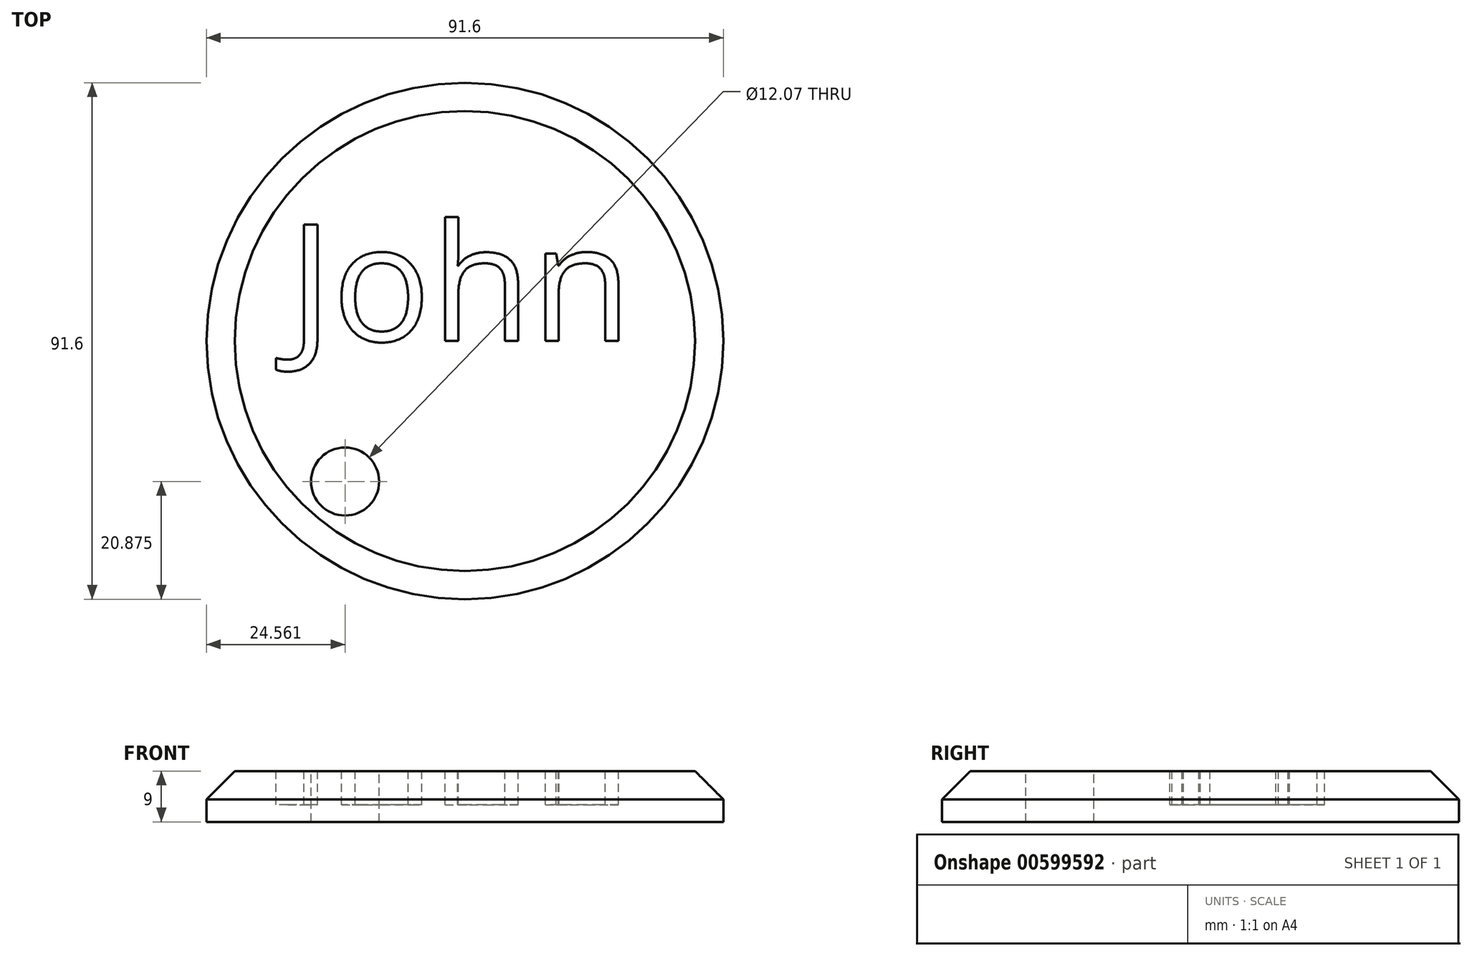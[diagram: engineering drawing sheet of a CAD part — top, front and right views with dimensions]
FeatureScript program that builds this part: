
annotation { "Feature Type Name" : "Feature", "Feature Type Description" : "" }
export const myFeature = defineFeature(function(context is Context, id is Id, definition is map)
    precondition{}
    {
        {
            var Q0;
            Q0=qCreatedBy(makeId("Top.planeOp"),FACE);
            var sketch = newSketch(context, id + "F0", { "sketchPlane" : qUnion([Q0])});
            skCircle(sketch, "E0", {"center": v(0, 0) * mm, "radius": 45.8 * mm});
            skSolve(sketch);
        }
        {
            var Q0;
            Q0=makeQuery(id+"F0.imprint","IMPRINT",FACE,{"disambiguationData":[TD([[makeQuery(id+"F0.imprint","IMPRINT",EDGE,{"derivedFrom":sQuery(id+"F0.wireOp",EDGE,"E0")}),1.0]])]});
            extrude(context, id + "F1", {"entities" : qUnion([Q0]), "depth" : 9 * mm, "offsetDistance" : 25.4 * mm});
        }
        {
            var Q0;
            Q0=makeQuery(id+"F1.opExtrude","CAP_FACE",FACE,{"disambiguationData":[OSD([sQuery(id+"F0.wireOp",EDGE,"E0")])],"isStart":false});
            chamfer(context, id + "F2", {"entities" : qUnion([Q0]), "width" : 5 * mm, "tangentPropagation" : true});
        }
        {
            var Q0;
            Q0=makeQuery(id+"F1.opExtrude","CAP_FACE",FACE,{"disambiguationData":[OSD([sQuery(id+"F0.wireOp",EDGE,"E0")])],"isStart":false});
            var sketch = newSketch(context, id + "F3", { "sketchPlane" : qUnion([Q0])});
            skText(sketch, "E1", { "text": "John\n", "fontName": "OpenSans-Regular.ttf"});
            const initialGuessF3  = {"E1": [-0.03123, 0, 1, 0, 0.02085]};
            skSetInitialGuess(sketch, initialGuessF3);
            skSolve(sketch);
        }
        {
            var Q0;
            Q0=makeQuery(id+"F3.imprint","IMPRINT",FACE,{"disambiguationData":[TD([[makeQuery(id+"F3.imprint","IMPRINT",EDGE,{"derivedFrom":sQuery(id+"F3.wireOp",EDGE,"E1.sketch_text.stroke-0")}),1.0]])]});
            var sketch = newSketch(context, id + "F4", { "sketchPlane" : qUnion([Q0])});
            skCircle(sketch, "E2", {"center": v(-21.24, -24.92) * mm, "radius": 6.03 * mm});
            skSolve(sketch);
        }
        {
            var Q0;
            Q0 = qSketchRegion(id + "F3", true);
            var Q1;
            Q1=sQuery(id+"F4.wireOp",EDGE,"E2");
            extrude(context, id + "F5", {"entities" : qUnion([Q0]), "operationType" : NewBodyOperationType.REMOVE, "surfaceEntities" : qUnion([Q1]), "oppositeDirection" : true, "depth" : 6 * mm, "offsetDistance" : 25 * mm});
        }
        {
            var Q0;
            Q0=makeQuery(id+"F4.imprint","IMPRINT",FACE,{"disambiguationData":[TD([[makeQuery(id+"F4.imprint","IMPRINT",EDGE,{"derivedFrom":sQuery(id+"F4.wireOp",EDGE,"E2")}),1.0]])]});
            extrude(context, id + "F6", {"entities" : qUnion([Q0]), "operationType" : NewBodyOperationType.REMOVE, "oppositeDirection" : true, "depth" : 11 * mm, "offsetDistance" : 25 * mm});
        }
    });
